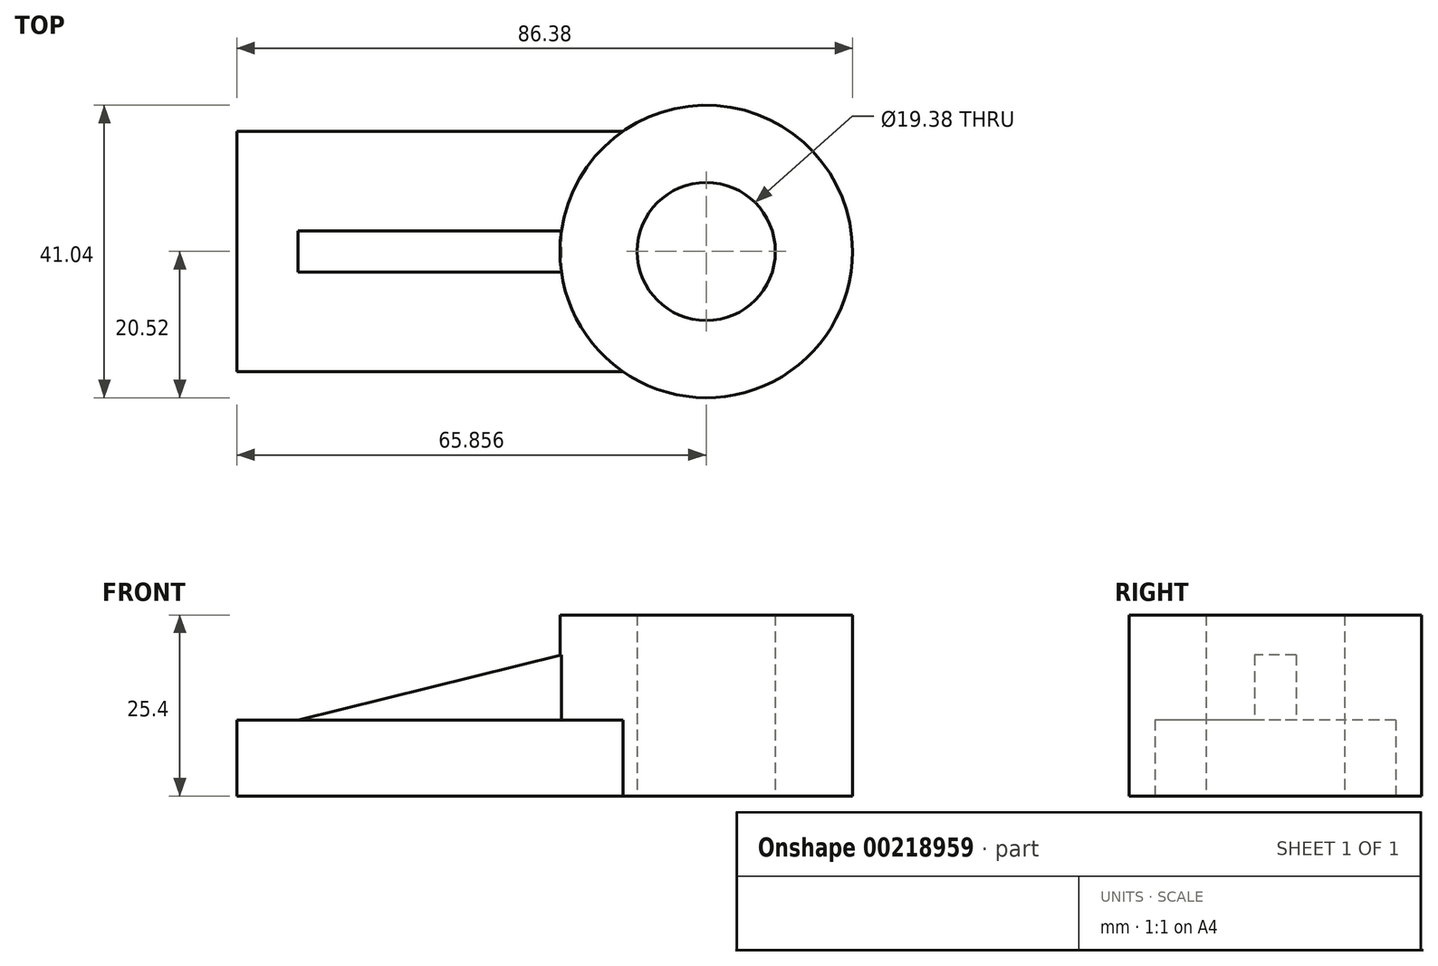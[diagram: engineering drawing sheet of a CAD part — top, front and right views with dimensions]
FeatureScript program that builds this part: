
annotation { "Feature Type Name" : "Feature", "Feature Type Description" : "" }
export const myFeature = defineFeature(function(context is Context, id is Id, definition is map)
    precondition{}
    {
        {
            var Q0;
            Q0=qCreatedBy(makeId("Top.planeOp"),FACE);
            var sketch = newSketch(context, id + "F0", { "sketchPlane" : qUnion([Q0])});
            skLineSegment(sketch, "E0.bottom", {"start": v(-1.18, 16.88) * mm, "end": v(-55.37, 16.88) * mm});
            skLineSegment(sketch, "E0.top", {"start": v(-1.18, -16.88) * mm, "end": v(-55.37, -16.88) * mm});
            skLineSegment(sketch, "E0.right", {"start": v(-55.37, 16.88) * mm, "end": v(-55.37, -16.88) * mm});
            skPoint(sketch, "E0.middle", {"position": v(-22.44, 0) * mm});
            skCircle(sketch, "E1", {"center": v(10.49, 0) * mm, "radius": 20.52 * mm});
            skCircle(sketch, "E2", {"center": v(10.49, 0) * mm, "radius": 9.7 * mm});
            skPoint(sketch, "E3.orphan", {"position": v(10.49, 16.88) * mm});
            skPoint(sketch, "E4.orphan", {"position": v(10.49, -16.88) * mm});
            skSolve(sketch);
        }
        {
            var Q0;
            {var subQ0=sQuery(id+"F0.wireOp",EDGE,"E0.bottom");Q0=makeQuery(id+"F0.imprint","IMPRINT",FACE,{"disambiguationData":[TD([[makeQuery(id+"F0.imprint","IMPRINT",EDGE,{"derivedFrom":subQ0}),1.0]])]});}
            extrude(context, id + "F1", {"entities" : qUnion([Q0]), "depth" : 10.67 * mm});
        }
        {
            var Q0;
            Q0=makeQuery(id+"F0.imprint","IMPRINT",FACE,{"disambiguationData":[TD([[makeQuery(id+"F0.imprint","IMPRINT",EDGE,{"derivedFrom":sQuery(id+"F0.wireOp",EDGE,"E2")}),-1.0]])]});
            extrude(context, id + "F2", {"entities" : qUnion([Q0]), "operationType" : NewBodyOperationType.ADD, "depth" : 25.4 * mm});
        }
        {
            var Q0;
            Q0=makeQuery(id+"F1.opExtrude","CAP_FACE",FACE,{"disambiguationData":[OSD([sQuery(id+"F0.wireOp",EDGE,"E0.bottom"),sQuery(id+"F0.wireOp",EDGE,"E0.top"),sQuery(id+"F0.wireOp",EDGE,"E0.right"),sQuery(id+"F0.wireOp",EDGE,"E1")])],"isStart":false});
            var sketch = newSketch(context, id + "F3", { "sketchPlane" : qUnion([Q0])});
            skLineSegment(sketch, "E5.bottom", {"start": v(-9.83, 2.9) * mm, "end": v(-46.8, 2.9) * mm});
            skLineSegment(sketch, "E5.top", {"start": v(-9.83, -2.9) * mm, "end": v(-46.8, -2.9) * mm});
            skLineSegment(sketch, "E5.left", {"start": v(-9.83, 2.9) * mm, "end": v(-9.83, -2.9) * mm});
            skLineSegment(sketch, "E5.right", {"start": v(-46.8, 2.9) * mm, "end": v(-46.8, -2.9) * mm});
            skPoint(sketch, "E5.middle", {"position": v(-28.31, 0) * mm});
            skSolve(sketch);
        }
        {
            var Q0;
            {var subQ0=sQuery(id+"F3.wireOp",EDGE,"E5.bottom");Q0=makeQuery(id+"F3.imprint","IMPRINT",FACE,{"disambiguationData":[TD([[makeQuery(id+"F3.imprint","IMPRINT",EDGE,{"derivedFrom":subQ0}),1.0]])]});}
            extrude(context, id + "F4", {"entities" : qUnion([Q0]), "operationType" : NewBodyOperationType.ADD, "depth" : 9.14 * mm});
        }
        {
            var Q0;
            Q0=makeQuery(id+"F4.opExtrude","SWEPT_FACE",FACE,{"disambiguationData":[OSD([sQuery(id+"F3.wireOp",EDGE,"E5.top")])]});
            var sketch = newSketch(context, id + "F5", { "sketchPlane" : qUnion([Q0])});
            skLineSegment(sketch, "E6", {"start": v(-9.83, 19.81) * mm, "end": v(-46.8, 10.67) * mm});
            skLineSegment(sketch, "E7", {"start": v(-46.8, 10.67) * mm, "end": v(-46.8, 19.81) * mm});
            skLineSegment(sketch, "E8", {"start": v(-46.8, 19.81) * mm, "end": v(-9.83, 19.81) * mm});
            skSolve(sketch);
        }
        {
            var Q0;
            Q0=makeQuery(id+"F5.imprint","IMPRINT",FACE,{"disambiguationData":[TD([[makeQuery(id+"F5.imprint","IMPRINT",EDGE,{"derivedFrom":sQuery(id+"F5.wireOp",EDGE,"E6")}),-1.0]])]});
            extrude(context, id + "F6", {"entities" : qUnion([Q0]), "operationType" : NewBodyOperationType.REMOVE, "endBound" : BoundingType.THROUGH_ALL, "oppositeDirection" : true, "depth" : 25.4 * mm});
        }
    });
